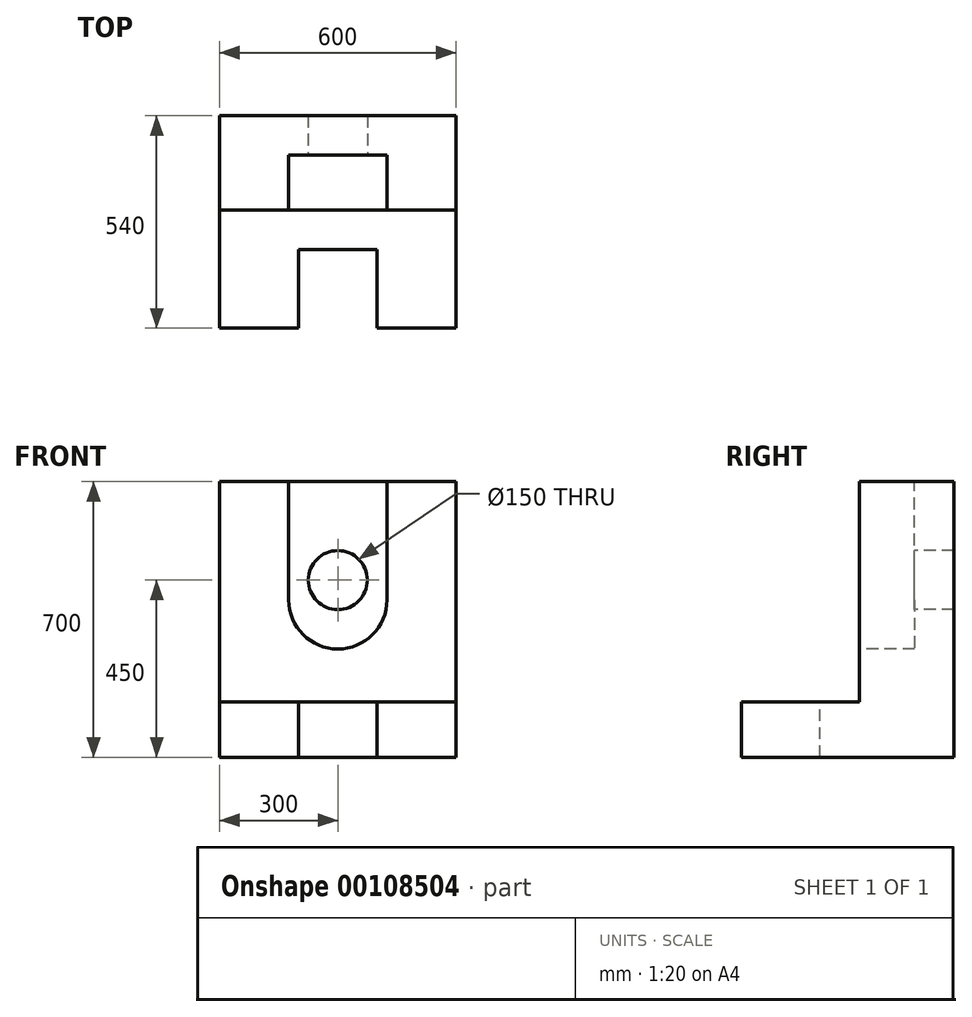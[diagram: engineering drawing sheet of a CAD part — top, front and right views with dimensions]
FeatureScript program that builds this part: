
annotation { "Feature Type Name" : "Feature", "Feature Type Description" : "" }
export const myFeature = defineFeature(function(context is Context, id is Id, definition is map)
    precondition{}
    {
        {
            var Q0;
            Q0=qCreatedBy(makeId("Front.planeOp"),FACE);
            var sketch = newSketch(context, id + "F0", { "sketchPlane" : qUnion([Q0])});
            skLineSegment(sketch, "E0.bottom", {"start": v(-300, -350) * mm, "end": v(300, -350) * mm});
            skLineSegment(sketch, "E0.top", {"start": v(-300, 350) * mm, "end": v(300, 350) * mm});
            skLineSegment(sketch, "E0.left", {"start": v(-300, -350) * mm, "end": v(-300, 350) * mm});
            skLineSegment(sketch, "E0.right", {"start": v(300, -350) * mm, "end": v(300, 350) * mm});
            skPoint(sketch, "E0.middle", {"position": v(0, 0) * mm});
            skSolve(sketch);
        }
        {
            var Q0;
            Q0 = qSketchRegion(id + "F0", true);
            extrude(context, id + "F1", {"entities" : qUnion([Q0]), "depth" : 540 * mm});
        }
        {
            var Q0;
            Q0=makeQuery(id+"F1.opExtrude","CAP_FACE",FACE,{"disambiguationData":[OSD([sQuery(id+"F0.wireOp",EDGE,"E0.bottom"),sQuery(id+"F0.wireOp",EDGE,"E0.top"),sQuery(id+"F0.wireOp",EDGE,"E0.left"),sQuery(id+"F0.wireOp",EDGE,"E0.right")])],"isStart":false});
            var sketch = newSketch(context, id + "F2", { "sketchPlane" : qUnion([Q0])});
            skLineSegment(sketch, "E1.bottom", {"start": v(300, 350) * mm, "end": v(-300, 350) * mm});
            skLineSegment(sketch, "E1.top", {"start": v(300, -210) * mm, "end": v(-300, -210) * mm});
            skLineSegment(sketch, "E1.left", {"start": v(300, 350) * mm, "end": v(300, -210) * mm});
            skLineSegment(sketch, "E1.right", {"start": v(-300, 350) * mm, "end": v(-300, -210) * mm});
            skSolve(sketch);
        }
        {
            var Q0;
            Q0 = qSketchRegion(id + "F2", true);
            extrude(context, id + "F3", {"entities" : qUnion([Q0]), "operationType" : NewBodyOperationType.REMOVE, "oppositeDirection" : true, "depth" : 300 * mm});
        }
        {
            var Q0;
            Q0=makeQuery(id+"F1.opExtrude","CAP_FACE",FACE,{"disambiguationData":[OSD([sQuery(id+"F0.wireOp",EDGE,"E0.bottom"),sQuery(id+"F0.wireOp",EDGE,"E0.top"),sQuery(id+"F0.wireOp",EDGE,"E0.left"),sQuery(id+"F0.wireOp",EDGE,"E0.right")])],"isStart":false});
            var sketch = newSketch(context, id + "F4", { "sketchPlane" : qUnion([Q0])});
            skLineSegment(sketch, "E2", {"start": v(0, -350) * mm, "end": v(0, -210) * mm, "construction": true});
            skPoint(sketch, "E3.middle", {"position": v(0, -280) * mm});
            skLineSegment(sketch, "E4.bottom", {"start": v(100, -350) * mm, "end": v(-100, -350) * mm});
            skLineSegment(sketch, "E4.top", {"start": v(100, -210) * mm, "end": v(-100, -210) * mm});
            skLineSegment(sketch, "E4.left", {"start": v(100, -350) * mm, "end": v(100, -210) * mm});
            skLineSegment(sketch, "E4.right", {"start": v(-100, -350) * mm, "end": v(-100, -210) * mm});
            skSolve(sketch);
        }
        {
            var Q0;
            Q0 = qSketchRegion(id + "F4", true);
            extrude(context, id + "F5", {"entities" : qUnion([Q0]), "operationType" : NewBodyOperationType.REMOVE, "oppositeDirection" : true, "depth" : 200 * mm});
        }
        {
            var Q0;
            Q0=makeQuery(id+"F3.boolean.opBoolean","COPY",FACE,{"derivedFrom":makeQuery(id+"F3.opExtrude","CAP_FACE",FACE,{"disambiguationData":[OSD([sQuery(id+"F2.wireOp",EDGE,"E1.bottom"),sQuery(id+"F2.wireOp",EDGE,"E1.top"),sQuery(id+"F2.wireOp",EDGE,"E1.left"),sQuery(id+"F2.wireOp",EDGE,"E1.right")])],"isStart":false})});
            var sketch = newSketch(context, id + "F6", { "sketchPlane" : qUnion([Q0])});
            skLineSegment(sketch, "E5.bottom", {"start": v(125, 50) * mm, "end": v(-125, 50) * mm});
            skLineSegment(sketch, "E5.top", {"start": v(125, 650) * mm, "end": v(-125, 650) * mm});
            skLineSegment(sketch, "E5.left", {"start": v(125, 50) * mm, "end": v(125, 650) * mm});
            skLineSegment(sketch, "E5.right", {"start": v(-125, 50) * mm, "end": v(-125, 650) * mm});
            skPoint(sketch, "E5.middle", {"position": v(0, 350) * mm});
            skPoint(sketch, "E6.center.orphan", {"position": v(0, 50) * mm});
            skArc(sketch, "E7", {"start": v(-125, 50) * mm, "mid": v(0, -75) * mm, "end": v(125, 50) * mm});
            skSolve(sketch);
        }
        {
            var Q0;
            Q0 = qSketchRegion(id + "F6", true);
            extrude(context, id + "F7", {"entities" : qUnion([Q0]), "operationType" : NewBodyOperationType.REMOVE, "oppositeDirection" : true, "depth" : 140 * mm});
        }
        {
            var Q0;
            Q0=makeQuery(id+"F7.boolean.opBoolean","COPY",FACE,{"derivedFrom":makeQuery(id+"F7.opExtrude","CAP_FACE",FACE,{"disambiguationData":[OSD([sQuery(id+"F6.wireOp",EDGE,"E5.top"),sQuery(id+"F6.wireOp",EDGE,"E5.left"),sQuery(id+"F6.wireOp",EDGE,"E5.right"),sQuery(id+"F6.wireOp",EDGE,"E7")])],"isStart":false})});
            var sketch = newSketch(context, id + "F8", { "sketchPlane" : qUnion([Q0])});
            skPoint(sketch, "E8.endSnap0", {"position": v(0, 350) * mm});
            skCircle(sketch, "E9", {"center": v(0, 100) * mm, "radius": 75 * mm});
            skSolve(sketch);
        }
        {
            var Q0;
            Q0 = qSketchRegion(id + "F8", true);
            extrude(context, id + "F9", {"entities" : qUnion([Q0]), "operationType" : NewBodyOperationType.REMOVE, "endBound" : BoundingType.THROUGH_ALL, "oppositeDirection" : true, "depth" : 25 * mm});
        }
    });
